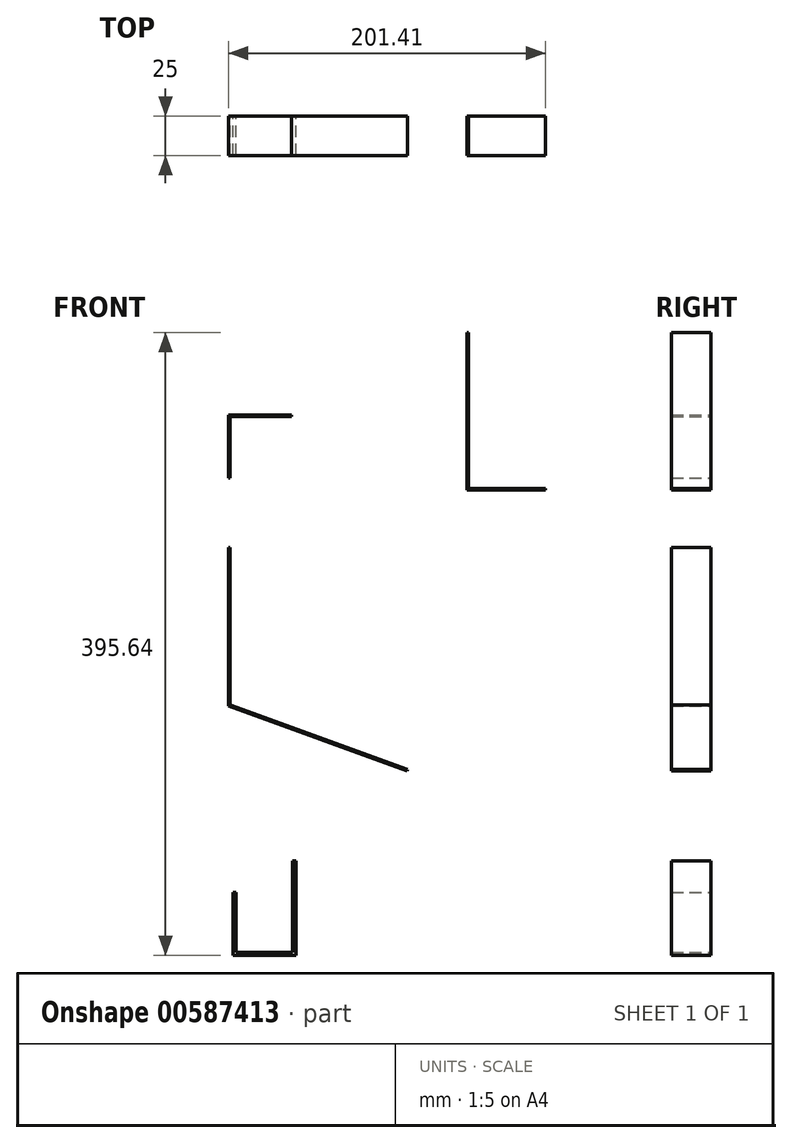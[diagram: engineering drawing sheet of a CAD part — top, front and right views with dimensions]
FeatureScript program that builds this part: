
annotation { "Feature Type Name" : "Feature", "Feature Type Description" : "" }
export const myFeature = defineFeature(function(context is Context, id is Id, definition is map)
    precondition{}
    {
        {
            var Q0;
            Q0=qCreatedBy(makeId("Front.planeOp"),FACE);
            var sketch = newSketch(context, id + "F0", { "sketchPlane" : qUnion([Q0])});
            skLineSegment(sketch, "E0", {"start": v(-30.79, 125.62) * mm, "end": v(-30.79, 25.62) * mm});
            skLineSegment(sketch, "E1", {"start": v(-30.79, 25.62) * mm, "end": v(81.98, -15.42) * mm});
            skLineSegment(sketch, "E2.0", {"start": v(-31.79, 24.92) * mm, "end": v(81.63, -16.36) * mm});
            skLineSegment(sketch, "E2.1", {"start": v(-31.79, 125.62) * mm, "end": v(-31.79, 24.92) * mm});
            skLineSegment(sketch, "E3", {"start": v(-31.79, 125.62) * mm, "end": v(-30.79, 125.62) * mm});
            skLineSegment(sketch, "E4", {"start": v(81.63, -16.36) * mm, "end": v(81.98, -15.42) * mm});
            skLineSegment(sketch, "E5", {"start": v(-29.04, -93.49) * mm, "end": v(-29.04, -133.49) * mm});
            skLineSegment(sketch, "E6", {"start": v(-29.04, -133.49) * mm, "end": v(10.96, -133.49) * mm});
            skLineSegment(sketch, "E7", {"start": v(10.96, -133.49) * mm, "end": v(10.96, -73.49) * mm});
            skLineSegment(sketch, "E8.0", {"start": v(8.96, -131.49) * mm, "end": v(8.96, -73.49) * mm});
            skLineSegment(sketch, "E8.1", {"start": v(-27.04, -131.49) * mm, "end": v(8.96, -131.49) * mm});
            skLineSegment(sketch, "E8.2", {"start": v(-27.04, -93.49) * mm, "end": v(-27.04, -131.49) * mm});
            skLineSegment(sketch, "E9", {"start": v(-29.04, -93.49) * mm, "end": v(-27.04, -93.49) * mm});
            skLineSegment(sketch, "E10", {"start": v(8.96, -73.49) * mm, "end": v(10.96, -73.49) * mm});
            skLineSegment(sketch, "E11", {"start": v(-31.79, 169.72) * mm, "end": v(-31.79, 209.72) * mm});
            skLineSegment(sketch, "E12", {"start": v(-31.79, 209.72) * mm, "end": v(8.21, 209.72) * mm});
            skLineSegment(sketch, "E13.0", {"start": v(-30.79, 208.72) * mm, "end": v(8.21, 208.72) * mm});
            skLineSegment(sketch, "E13.1", {"start": v(-30.79, 169.72) * mm, "end": v(-30.79, 208.72) * mm});
            skLineSegment(sketch, "E14", {"start": v(-31.79, 169.72) * mm, "end": v(-30.79, 169.72) * mm});
            skLineSegment(sketch, "E15", {"start": v(8.21, 209.72) * mm, "end": v(8.21, 208.72) * mm});
            skSolve(sketch);
        }
        {
            var Q0;
            Q0 = qSketchRegion(id + "F0", true);
            extrude(context, id + "F1", {"entities" : qUnion([Q0]), "depth" : 25 * mm, "offsetDistance" : 25 * mm});
        }
        {
            var Q0;
            Q0=qCreatedBy(makeId("Front.planeOp"),FACE);
            var sketch = newSketch(context, id + "F2", { "sketchPlane" : qUnion([Q0])});
            skLineSegment(sketch, "E16", {"start": v(119.62, 262.15) * mm, "end": v(119.62, 162.15) * mm});
            skLineSegment(sketch, "E17", {"start": v(119.62, 162.15) * mm, "end": v(169.62, 162.15) * mm});
            skLineSegment(sketch, "E18.0", {"start": v(120.62, 163.15) * mm, "end": v(169.62, 163.15) * mm});
            skLineSegment(sketch, "E18.1", {"start": v(120.62, 262.15) * mm, "end": v(120.62, 163.15) * mm});
            skLineSegment(sketch, "E19", {"start": v(119.62, 262.15) * mm, "end": v(120.62, 262.15) * mm});
            skLineSegment(sketch, "E20", {"start": v(169.62, 163.15) * mm, "end": v(169.62, 162.15) * mm});
            skSolve(sketch);
        }
        {
            var Q0;
            Q0=makeQuery(id+"F2.imprint","IMPRINT",FACE,{"disambiguationData":[TD([[makeQuery(id+"F2.imprint","IMPRINT",EDGE,{"derivedFrom":sQuery(id+"F2.wireOp",EDGE,"E16")}),1.0]])]});
            extrude(context, id + "F3", {"entities" : qUnion([Q0]), "depth" : 25 * mm, "offsetDistance" : 25 * mm});
        }
    });
